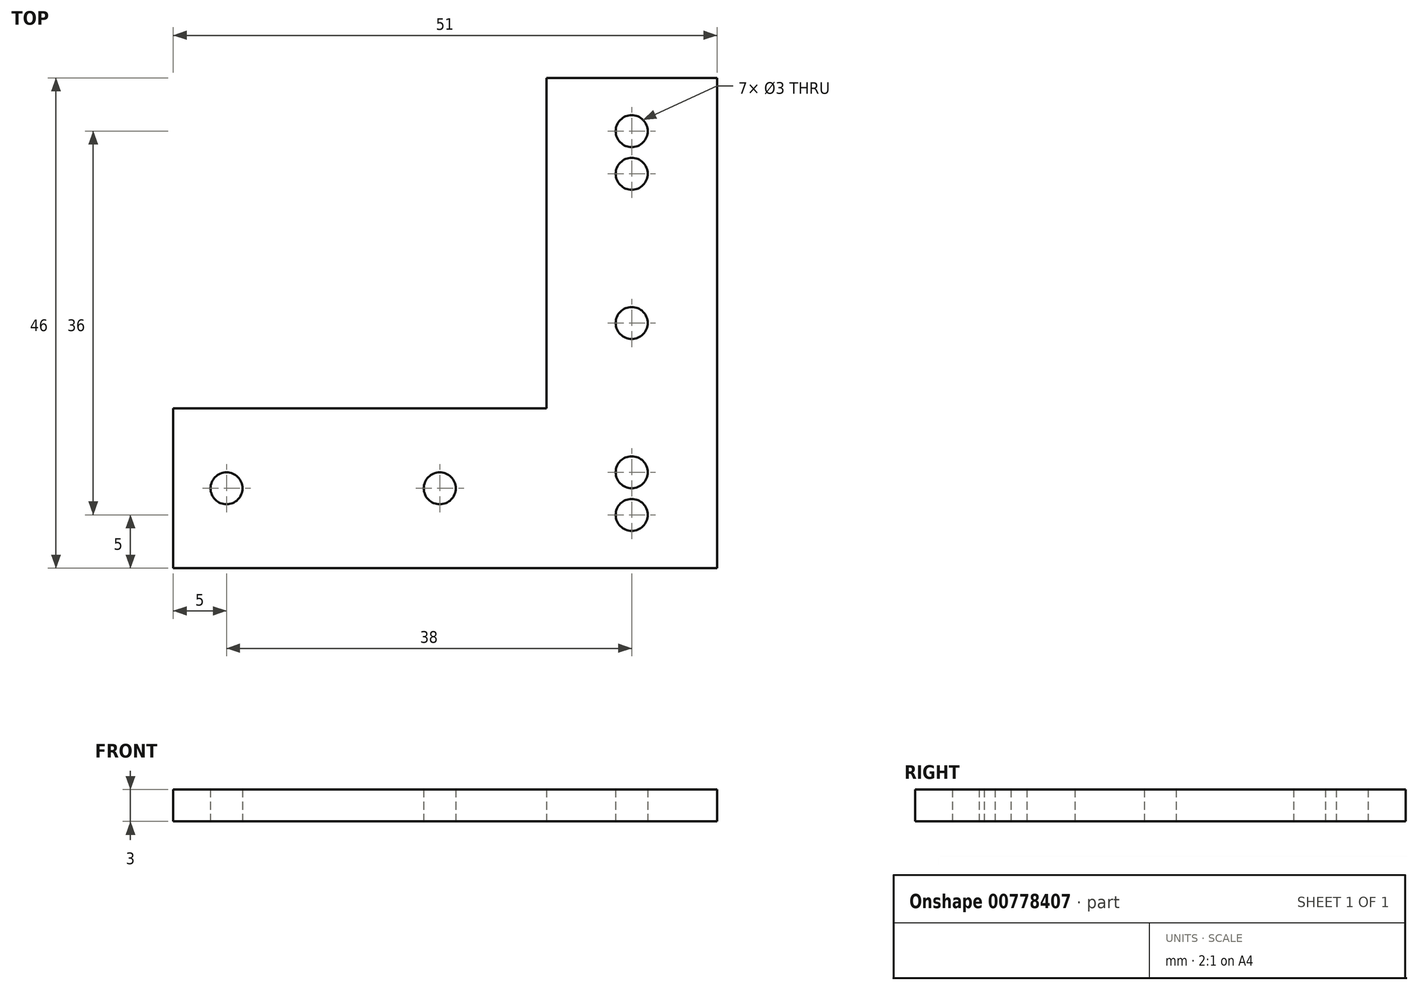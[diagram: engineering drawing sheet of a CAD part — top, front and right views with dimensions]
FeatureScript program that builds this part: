
annotation { "Feature Type Name" : "Feature", "Feature Type Description" : "" }
export const myFeature = defineFeature(function(context is Context, id is Id, definition is map)
    precondition{}
    {
        {
            var Q0;
            Q0=qCreatedBy(makeId("Top.planeOp"),FACE);
            var sketch = newSketch(context, id + "F0", { "sketchPlane" : qUnion([Q0])});
            skLineSegment(sketch, "E0.bottom", {"start": v(0, 0) * mm, "end": v(-35, 0) * mm});
            skLineSegment(sketch, "E0.top", {"start": v(0, -15) * mm, "end": v(-35, -15) * mm});
            skLineSegment(sketch, "E0.right", {"start": v(-35, 0) * mm, "end": v(-35, -15) * mm});
            skLineSegment(sketch, "E1", {"start": v(-10, -7.5) * mm, "end": v(-30, -7.5) * mm, "construction": true});
            skLineSegment(sketch, "E2.top", {"start": v(0, 31) * mm, "end": v(16, 31) * mm});
            skLineSegment(sketch, "E3", {"start": v(8, 8) * mm, "end": v(8, 22) * mm, "construction": true});
            skPoint(sketch, "E4", {"position": v(8, -6) * mm});
            skLineSegment(sketch, "E5.top", {"start": v(0, -15) * mm, "end": v(16, -15) * mm});
            skLineSegment(sketch, "E5.left", {"start": v(0, -15) * mm, "end": v(0, -15) * mm});
            skLineSegment(sketch, "E5.right", {"start": v(16, 31) * mm, "end": v(16, -15) * mm});
            skLineSegment(sketch, "E6", {"start": v(8, 8) * mm, "end": v(8, -6) * mm, "construction": true});
            skLineSegment(sketch, "E7", {"start": v(0, 0) * mm, "end": v(0, 31) * mm});
            skPoint(sketch, "E8", {"position": v(8, 26) * mm});
            skPoint(sketch, "E9", {"position": v(8, -10) * mm});
            skSolve(sketch);
        }
        {
            var Q0;
            {var subQ0=sQuery(id+"F0.wireOp",EDGE,"E0.bottom");Q0=makeQuery(id+"F0.imprint","IMPRINT",FACE,{"disambiguationData":[TD([[makeQuery(id+"F0.imprint","IMPRINT",EDGE,{"derivedFrom":subQ0}),1.0]])]});}
            var Q1;
            {var subQ3=sQuery(id+"F0.wireOp",EDGE,"E2.bottom");Q1=makeQuery(id+"F0.imprint","IMPRINT",FACE,{"disambiguationData":[TD([[makeQuery(id+"F0.imprint","IMPRINT",EDGE,{"derivedFrom":subQ3}),1.0]])]});}
            extrude(context, id + "F1", {"entities" : qUnion([Q0, Q1]), "depth" : 3 * mm, "offsetDistance" : 25 * mm});
        }
        {
            var Q0;
            Q0=sQuery(id+"F0.wireOp",VERTEX,"E3.start");
            var Q1;
            Q1=sQuery(id+"F0.wireOp",VERTEX,"E3.end");
            var Q2;
            Q2=sQuery(id+"F0.wireOp",VERTEX,"E1.start");
            var Q3;
            Q3=sQuery(id+"F0.wireOp",VERTEX,"E1.end");
            var Q4;
            Q4=sQuery(id+"F0.wireOp",VERTEX,"E4");
            var Q5;
            Q5=sQuery(id+"F0.wireOp",VERTEX,"E8");
            var Q6;
            Q6=sQuery(id+"F0.wireOp",VERTEX,"E9");
            var Q7;
            Q7=makeQuery(id+"F1.opExtrude","SWEPT_BODY",BODY,{"disambiguationData":[OSD([sQuery(id+"F0.wireOp",EDGE,"E0.bottom"),sQuery(id+"F0.wireOp",EDGE,"E0.top"),sQuery(id+"F0.wireOp",EDGE,"E0.right"),sQuery(id+"F0.wireOp",EDGE,"E2.bottom"),sQuery(id+"F0.wireOp",EDGE,"E2.top"),sQuery(id+"F0.wireOp",EDGE,"E2.left"),sQuery(id+"F0.wireOp",EDGE,"E2.right")])]});
            hole(context, id + "F2", {"style" : HoleStyle.SIMPLE, "endStyle" : HoleEndStyle.THROUGH, "oppositeDirection" : true, "holeDiameter" : 3 * mm, "majorDiameter" : 5 * mm, "isTappedThrough" : true, "tappedDepth" : 12 * mm, "tapClearance" : 3, "locations" : qUnion([Q0, Q1, Q2, Q3, Q4, Q5, Q6]), "scope" : qUnion([Q7])});
        }
    });
